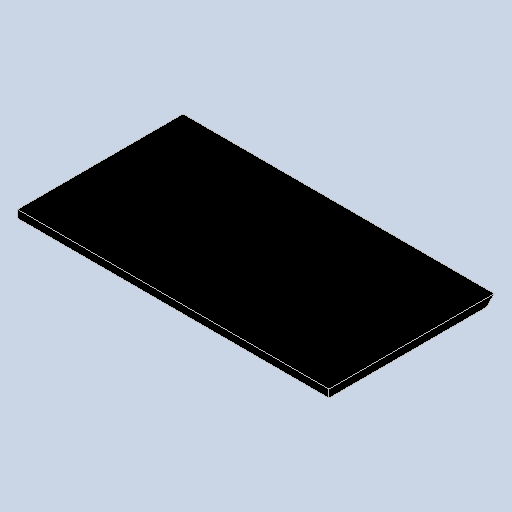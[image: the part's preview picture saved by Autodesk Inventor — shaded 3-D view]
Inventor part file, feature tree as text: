
AUTODESK INVENTOR PART (.ipt)
format: ipt  version: 2022 (Build 260153000, 153)  size: 102,912 bytes
history: native  units: mm
features: other x1, extrude x1, chamfer x1, sketch x1
ambient origin geometry x8: Origin, YZ Plane, XZ Plane, XY Plane, X Axis, Y Axis, Z Axis, Center Point
bodies: Body1 (feature_tree)
feature tree (4):
  other  "ソリッド1"
  extrude  "押し出し1"  Depth=80.0mm
  chamfer  "面取り4"  Distance=42.5mm
  sketch  "スケッチ1"
